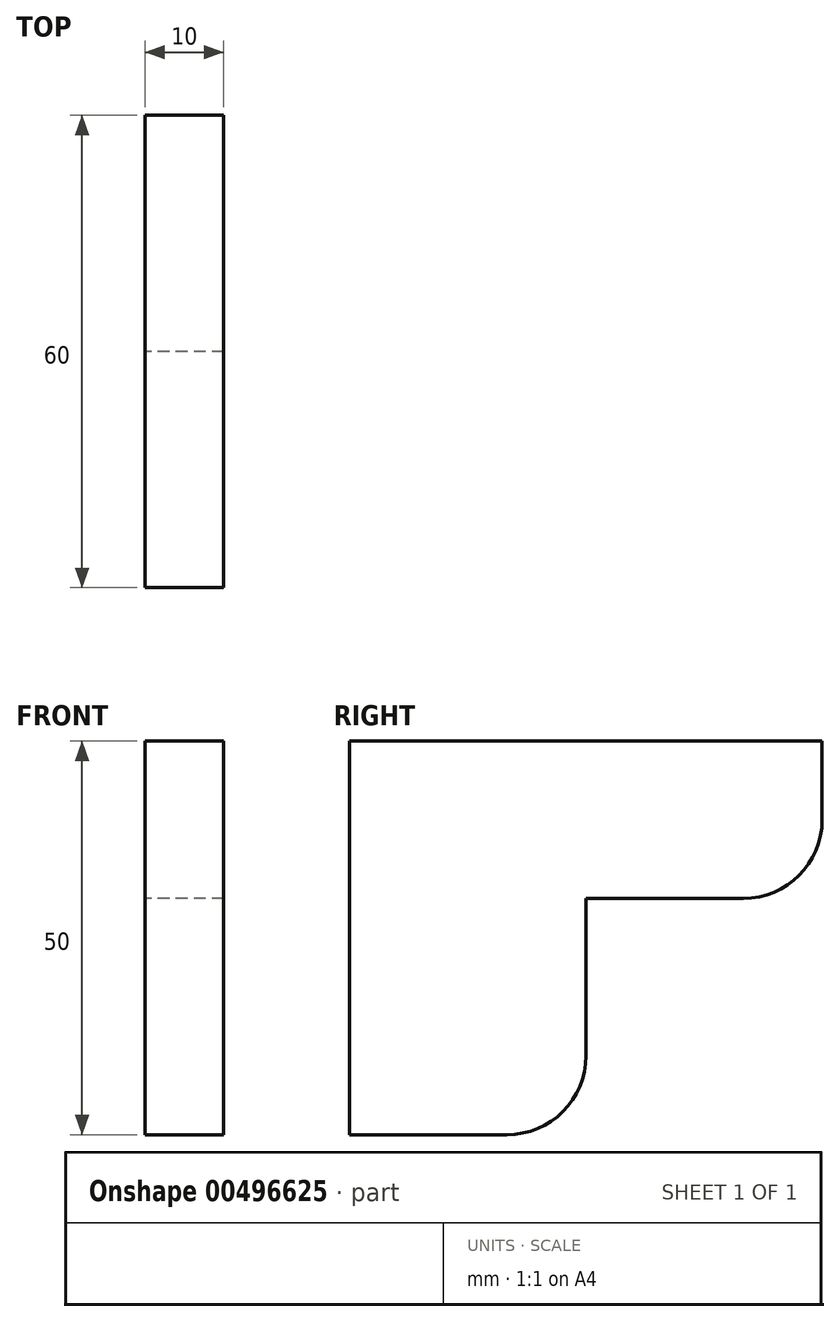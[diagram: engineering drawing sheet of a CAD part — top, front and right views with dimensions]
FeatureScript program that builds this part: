
annotation { "Feature Type Name" : "Feature", "Feature Type Description" : "" }
export const myFeature = defineFeature(function(context is Context, id is Id, definition is map)
    precondition{}
    {
        {
            var Q0;
            Q0=qCreatedBy(makeId("Right.planeOp"),FACE);
            var sketch = newSketch(context, id + "F0", { "sketchPlane" : qUnion([Q0])});
            skLineSegment(sketch, "E0", {"start": v(0, 0) * mm, "end": v(0, 50) * mm});
            skLineSegment(sketch, "E1", {"start": v(0, 50) * mm, "end": v(20, 50) * mm});
            skLineSegment(sketch, "E2", {"start": v(20, 50) * mm, "end": v(20, 40) * mm});
            skLineSegment(sketch, "E3", {"start": v(20, 40) * mm, "end": v(0, 40) * mm});
            skLineSegment(sketch, "E4", {"start": v(20, 50) * mm, "end": v(50, 50) * mm});
            skLineSegment(sketch, "E5", {"start": v(50, 50) * mm, "end": v(50, 40) * mm});
            skLineSegment(sketch, "E6", {"start": v(50, 40) * mm, "end": v(20, 40) * mm});
            skLineSegment(sketch, "E7", {"start": v(50, 50) * mm, "end": v(60, 50) * mm});
            skLineSegment(sketch, "E8", {"start": v(50, 40) * mm, "end": v(60, 40) * mm});
            skLineSegment(sketch, "E9", {"start": v(60, 40) * mm, "end": v(60, 40) * mm});
            skLineSegment(sketch, "E10", {"start": v(50, 30) * mm, "end": v(40, 30) * mm});
            skLineSegment(sketch, "E11", {"start": v(0, 0) * mm, "end": v(10, 0) * mm});
            skLineSegment(sketch, "E12", {"start": v(10, 0) * mm, "end": v(20, 0) * mm});
            skLineSegment(sketch, "E13", {"start": v(10, 0) * mm, "end": v(10, 40) * mm});
            skLineSegment(sketch, "E14", {"start": v(30, 10) * mm, "end": v(30, 30) * mm});
            skLineSegment(sketch, "E15", {"start": v(30, 30) * mm, "end": v(40, 30) * mm});
            skPoint(sketch, "E16.visualSharp", {"position": v(30, 0) * mm});
            skArc(sketch, "E16.filletArc", {"start": v(20, 0) * mm, "mid": v(27.07, 2.93) * mm, "end": v(30, 10) * mm});
            skPoint(sketch, "E17.visualSharp", {"position": v(60, 30) * mm});
            skArc(sketch, "E17.filletArc", {"start": v(50, 30) * mm, "mid": v(57.07, 32.93) * mm, "end": v(60, 40) * mm});
            skLineSegment(sketch, "E18", {"start": v(60, 50) * mm, "end": v(60, 40) * mm});
            skSolve(sketch);
        }
        {
            var Q0;
            {var subQ0=sQuery(id+"F0.wireOp",EDGE,"E11");Q0=makeQuery(id+"F0.imprint","IMPRINT",FACE,{"disambiguationData":[TD([[makeQuery(id+"F0.imprint","IMPRINT",EDGE,{"derivedFrom":subQ0}),1.0]])]});}
            var Q1;
            Q1=makeQuery(id+"F0.imprint","IMPRINT",FACE,{"disambiguationData":[TD([[makeQuery(id+"F0.imprint","IMPRINT",EDGE,{"derivedFrom":sQuery(id+"F0.wireOp",EDGE,"E5")}),1.0]])]});
            var Q2;
            {var subQ3=sQuery(id+"F0.wireOp",EDGE,"E1");Q2=makeQuery(id+"F0.imprint","IMPRINT",FACE,{"disambiguationData":[TD([[makeQuery(id+"F0.imprint","IMPRINT",EDGE,{"derivedFrom":subQ3}),-1.0]])]});}
            var Q3;
            Q3=makeQuery(id+"F0.imprint","IMPRINT",FACE,{"disambiguationData":[TD([[makeQuery(id+"F0.imprint","IMPRINT",EDGE,{"derivedFrom":sQuery(id+"F0.wireOp",EDGE,"E2")}),1.0]])]});
            var Q4;
            {var subQ0=sQuery(id+"F0.wireOp",EDGE,"E6");Q4=makeQuery(id+"F0.imprint","IMPRINT",FACE,{"disambiguationData":[TD([[makeQuery(id+"F0.imprint","IMPRINT",EDGE,{"derivedFrom":subQ0}),1.0]])]});}
            extrude(context, id + "F1", {"entities" : qUnion([Q0, Q1, Q2, Q3, Q4]), "depth" : 10 * mm, "offsetDistance" : 25 * mm});
        }
    });
